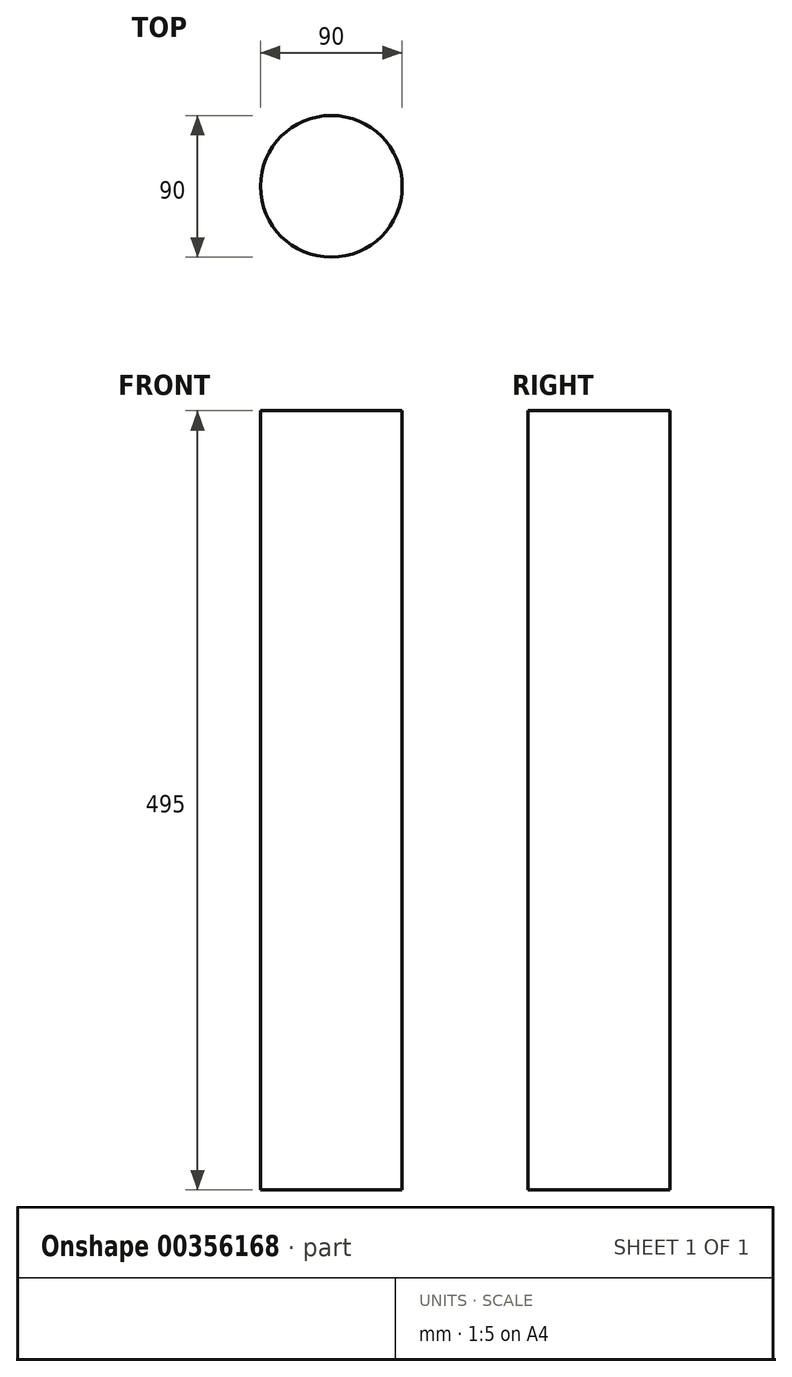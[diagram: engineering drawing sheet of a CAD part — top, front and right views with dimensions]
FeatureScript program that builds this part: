
annotation { "Feature Type Name" : "Feature", "Feature Type Description" : "" }
export const myFeature = defineFeature(function(context is Context, id is Id, definition is map)
    precondition{}
    {
        {
            var Q0;
            Q0=qCreatedBy(makeId("Front.planeOp"),FACE);
            var sketch = newSketch(context, id + "F0", { "sketchPlane" : qUnion([Q0])});
            skLineSegment(sketch, "E0.bottom", {"start": v(0, 500) * mm, "end": v(-50, 500) * mm});
            skLineSegment(sketch, "E0.top", {"start": v(0, 0) * mm, "end": v(-50, 0) * mm});
            skLineSegment(sketch, "E0.left", {"start": v(0, 500) * mm, "end": v(0, 0) * mm});
            skLineSegment(sketch, "E0.right", {"start": v(-50, 500) * mm, "end": v(-50, 0) * mm});
            skLineSegment(sketch, "E1.bottom", {"start": v(-50, 60) * mm, "end": v(-50, 60) * mm});
            skLineSegment(sketch, "E1.top", {"start": v(-50, 0) * mm, "end": v(-50, 0) * mm});
            skLineSegment(sketch, "E1.left", {"start": v(-50, 60) * mm, "end": v(-50, 0) * mm});
            skLineSegment(sketch, "E1.right", {"start": v(-55, 55) * mm, "end": v(-55, 5) * mm});
            skPoint(sketch, "E2.visualSharp", {"position": v(-55, 0) * mm});
            skArc(sketch, "E2.filletArc", {"start": v(-55, 5) * mm, "mid": v(-53.54, 1.46) * mm, "end": v(-50, 0) * mm});
            skLineSegment(sketch, "E3.bottom", {"start": v(-45, 500) * mm, "end": v(0, 500) * mm});
            skLineSegment(sketch, "E3.top", {"start": v(-45, 5) * mm, "end": v(0, 5) * mm});
            skLineSegment(sketch, "E3.left", {"start": v(-45, 500) * mm, "end": v(-45, 5) * mm});
            skPoint(sketch, "E4.visualSharp", {"position": v(-55, 60) * mm});
            skArc(sketch, "E4.filletArc", {"start": v(-50, 60) * mm, "mid": v(-53.54, 58.54) * mm, "end": v(-55, 55) * mm});
            skSolve(sketch);
        }
        {
            var Q0;
            Q0=makeQuery(id+"F0.imprint","IMPRINT",FACE,{"disambiguationData":[TD([[makeQuery(id+"F0.imprint","IMPRINT",EDGE,{"derivedFrom":sQuery(id+"F0.wireOp",EDGE,"E1.left")}),-1.0]])]});
            var Q1;
            Q1=makeQuery(id+"F0.imprint","IMPRINT",FACE,{"disambiguationData":[TD([[makeQuery(id+"F0.imprint","IMPRINT",EDGE,{"derivedFrom":sQuery(id+"F0.wireOp",EDGE,"E0.bottom")}),1.0]])]});
            var Q2;
            Q2=sQuery(id+"F0.wireOp",EDGE,"E0.left");
            revolve(context, id + "F1", {"entities" : qUnion([Q0, Q1]), "axis" : qUnion([Q2]), "revolveType" : RevolveType.FULL});
        }
    });
